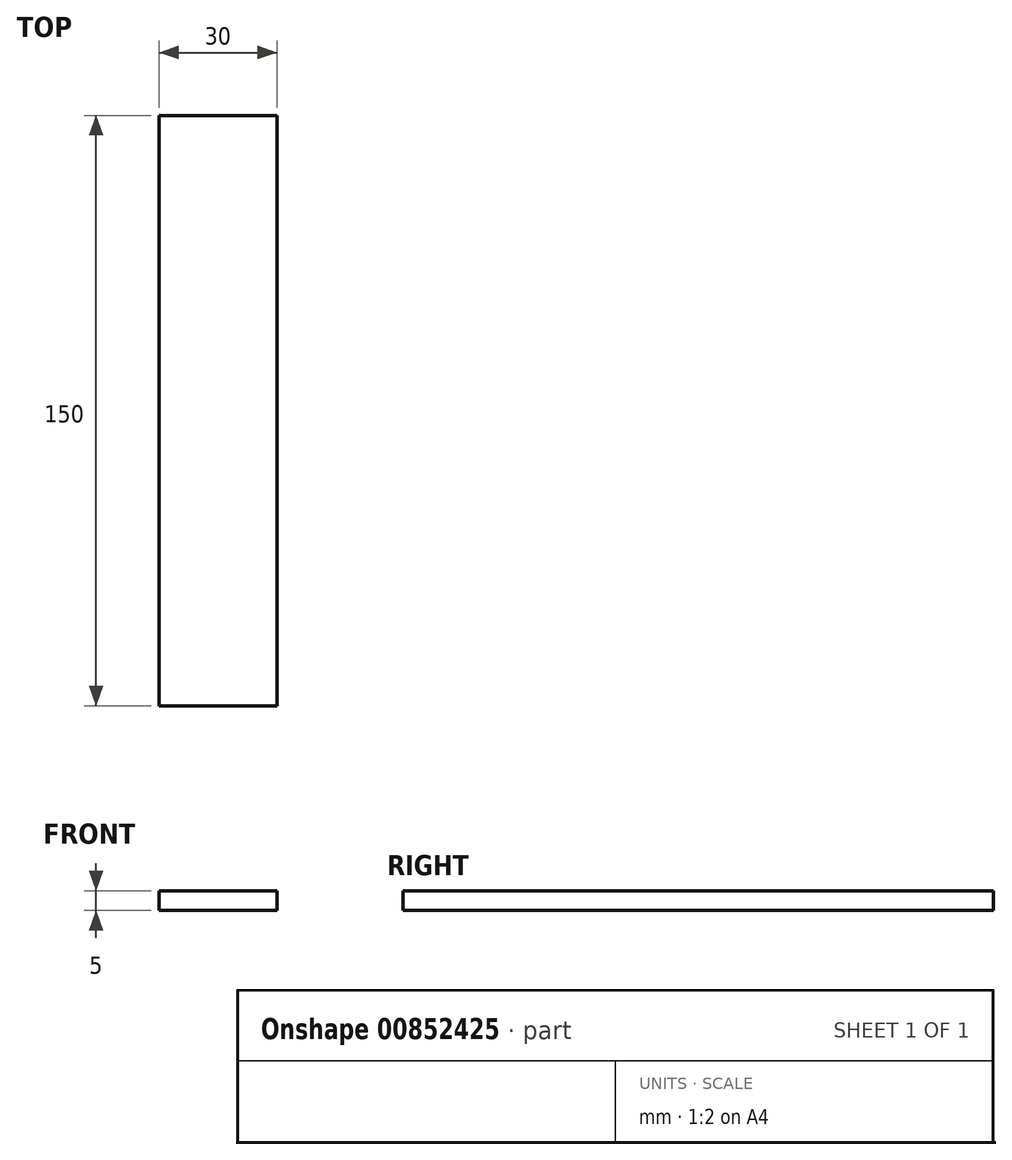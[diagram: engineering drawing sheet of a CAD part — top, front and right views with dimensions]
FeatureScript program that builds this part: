
annotation { "Feature Type Name" : "Feature", "Feature Type Description" : "" }
export const myFeature = defineFeature(function(context is Context, id is Id, definition is map)
    precondition{}
    {
        {
            var Q0;
            Q0=qCreatedBy(makeId("Front.planeOp"),FACE);
            var sketch = newSketch(context, id + "F0", { "sketchPlane" : qUnion([Q0])});
            skLineSegment(sketch, "E0", {"start": v(3, -15) * mm, "end": v(30, -15) * mm});
            skLineSegment(sketch, "E1", {"start": v(30, -15) * mm, "end": v(30, -20) * mm});
            skLineSegment(sketch, "E2", {"start": v(30, -20) * mm, "end": v(0, -20) * mm});
            skLineSegment(sketch, "E3", {"start": v(0, -20) * mm, "end": v(0, -15) * mm});
            skLineSegment(sketch, "E4", {"start": v(0, -15) * mm, "end": v(3, -15) * mm});
            skSolve(sketch);
        }
        {
            var Q0;
            Q0=makeQuery(id+"F0.imprint","IMPRINT",FACE,{"disambiguationData":[TD([[makeQuery(id+"F0.imprint","IMPRINT",EDGE,{"derivedFrom":sQuery(id+"F0.wireOp",EDGE,"vVoRWk9A-FnrN-TGXc-otKg-ayrUB0VCOAvG")}),-1.0]])]});
            var Q1;
            Q1=makeQuery(id+"F0.imprint","IMPRINT",FACE,{"disambiguationData":[TD([[makeQuery(id+"F0.imprint","IMPRINT",EDGE,{"derivedFrom":sQuery(id+"F0.wireOp",EDGE,"E0")}),-1.0]])]});
            extrude(context, id + "F1", {"entities" : qUnion([Q0, Q1]), "depth" : 150 * mm, "offsetDistance" : 25 * mm});
        }
    });
